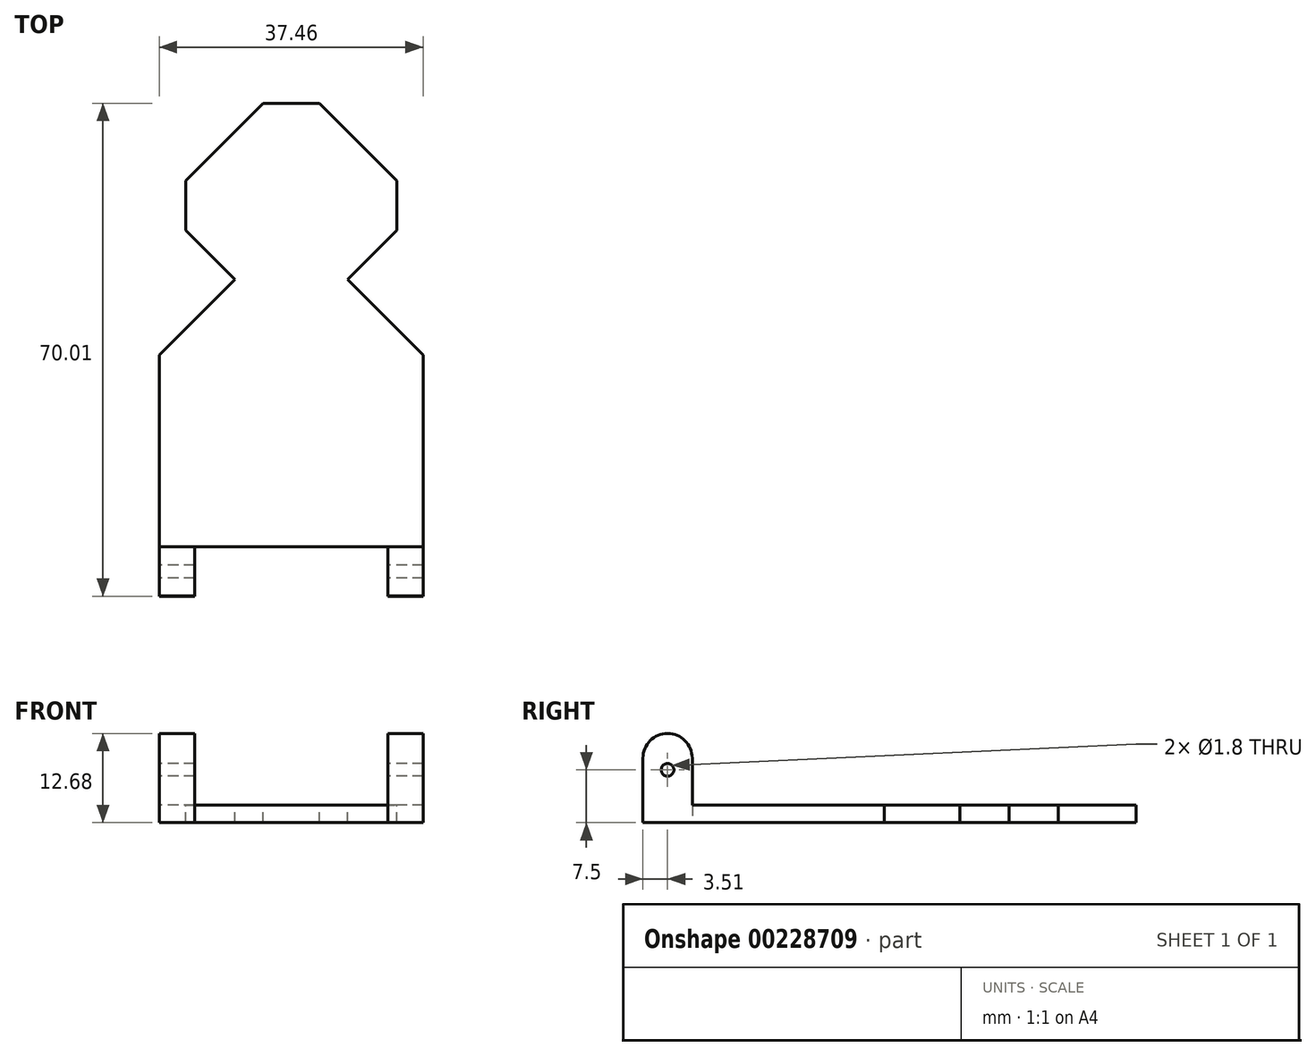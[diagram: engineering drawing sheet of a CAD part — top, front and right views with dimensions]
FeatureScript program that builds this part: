
annotation { "Feature Type Name" : "Feature", "Feature Type Description" : "" }
export const myFeature = defineFeature(function(context is Context, id is Id, definition is map)
    precondition{}
    {
        {
            var Q0;
            Q0=qCreatedBy(makeId("Right.planeOp"),FACE);
            var sketch = newSketch(context, id + "F0", { "sketchPlane" : qUnion([Q0])});
            skLineSegment(sketch, "E0.top", {"start": v(35, 2.5) * mm, "end": v(-35, 2.5) * mm});
            skLineSegment(sketch, "E0.left", {"start": v(35, 0) * mm, "end": v(35, 2.5) * mm});
            skPoint(sketch, "E0.middle", {"position": v(0, 0) * mm});
            skLineSegment(sketch, "E1.bottom", {"start": v(-28, 2.5) * mm, "end": v(-35, 2.5) * mm});
            skLineSegment(sketch, "E1.left", {"start": v(-28, 2.5) * mm, "end": v(-28, 9.18) * mm});
            skLineSegment(sketch, "E1.right", {"start": v(-35, 2.5) * mm, "end": v(-35, 9.18) * mm});
            skCircle(sketch, "E2", {"center": v(-31.5, 7.5) * mm, "radius": 0.9 * mm});
            skArc(sketch, "E3", {"start": v(-28, 9.18) * mm, "mid": v(-31.5, 12.68) * mm, "end": v(-35, 9.18) * mm});
            skLineSegment(sketch, "E4", {"start": v(35, 0) * mm, "end": v(-35, 0) * mm});
            skLineSegment(sketch, "E5", {"start": v(-35, 0) * mm, "end": v(-35, 2.5) * mm});
            skSolve(sketch);
        }
        {
            var Q0;
            {var subQ1=sQuery(id+"F0.wireOp",EDGE,"E1.left");Q0=makeQuery(id+"F0.imprint","IMPRINT",FACE,{"disambiguationData":[TD([[makeQuery(id+"F0.imprint","IMPRINT",EDGE,{"derivedFrom":subQ1}),1.0]])]});}
            var Q1;
            {var subQ0=sQuery(id+"F0.wireOp",EDGE,"E0.left");Q1=makeQuery(id+"F0.imprint","IMPRINT",FACE,{"disambiguationData":[TD([[makeQuery(id+"F0.imprint","IMPRINT",EDGE,{"derivedFrom":subQ0}),1.0]])]});}
            extrude(context, id + "F1", {"entities" : qUnion([Q0, Q1]), "depth" : 18.73 * mm, "hasSecondDirection" : true, "secondDirectionOppositeDirection" : true, "secondDirectionDepth" : 18.73 * mm});
        }
        {
            var Q0;
            Q0=qCreatedBy(makeId("Top.planeOp"),FACE);
            var sketch = newSketch(context, id + "F2", { "sketchPlane" : qUnion([Q0])});
            skLineSegment(sketch, "E6.bottom", {"start": v(13.73, -28) * mm, "end": v(-13.73, -28) * mm});
            skLineSegment(sketch, "E6.top", {"start": v(13.73, -38) * mm, "end": v(-13.73, -38) * mm});
            skLineSegment(sketch, "E6.left", {"start": v(13.73, -28) * mm, "end": v(13.73, -38) * mm});
            skLineSegment(sketch, "E6.right", {"start": v(-13.73, -28) * mm, "end": v(-13.73, -38) * mm});
            skPoint(sketch, "E6.middle", {"position": v(0, -33) * mm});
            skLineSegment(sketch, "E7.bottom", {"start": v(-15, 10) * mm, "end": v(-25, 10) * mm});
            skLineSegment(sketch, "E7.top", {"start": v(-15, 31) * mm, "end": v(-25, 31) * mm});
            skLineSegment(sketch, "E7.left", {"start": v(-15, 10) * mm, "end": v(-15, 31) * mm});
            skLineSegment(sketch, "E7.right", {"start": v(-25, 10) * mm, "end": v(-25, 31) * mm});
            skPoint(sketch, "E7.middle", {"position": v(-20, 20.5) * mm});
            skLineSegment(sketch, "E8.MirrorCS", {"start": v(15, 10) * mm, "end": v(15, 31) * mm});
            skLineSegment(sketch, "E9.MirrorCS", {"start": v(15, 10) * mm, "end": v(25, 10) * mm});
            skLineSegment(sketch, "E10.MirrorCS", {"start": v(25, 10) * mm, "end": v(25, 31) * mm});
            skLineSegment(sketch, "E11.MirrorCS", {"start": v(15, 31) * mm, "end": v(25, 31) * mm});
            skLineSegment(sketch, "E12", {"start": v(-15, 24) * mm, "end": v(-8, 31) * mm});
            skLineSegment(sketch, "E13", {"start": v(-8, 31) * mm, "end": v(-15, 31) * mm});
            skLineSegment(sketch, "E14", {"start": v(-15, 10) * mm, "end": v(-8, 10) * mm});
            skLineSegment(sketch, "E15", {"start": v(-8, 10) * mm, "end": v(-15, 17) * mm});
            skLineSegment(sketch, "E16.MirrorCS", {"start": v(8, 31) * mm, "end": v(15, 31) * mm});
            skLineSegment(sketch, "E17.MirrorCS", {"start": v(15, 24) * mm, "end": v(8, 31) * mm});
            skLineSegment(sketch, "E18.MirrorCS", {"start": v(8, 10) * mm, "end": v(15, 17) * mm});
            skLineSegment(sketch, "E19.MirrorCS", {"start": v(15, 10) * mm, "end": v(8, 10) * mm});
            skLineSegment(sketch, "E20", {"start": v(-8, 31) * mm, "end": v(-1, 38) * mm});
            skLineSegment(sketch, "E21", {"start": v(-1, 38) * mm, "end": v(-25, 38) * mm});
            skLineSegment(sketch, "E22", {"start": v(-25, 38) * mm, "end": v(-25, 31) * mm});
            skLineSegment(sketch, "E23.MirrorCS", {"start": v(8, 31) * mm, "end": v(1, 38) * mm});
            skLineSegment(sketch, "E24.MirrorCS", {"start": v(1, 38) * mm, "end": v(25, 38) * mm});
            skLineSegment(sketch, "E25.MirrorCS", {"start": v(25, 38) * mm, "end": v(25, 31) * mm});
            skLineSegment(sketch, "E26", {"start": v(-8, 10) * mm, "end": v(-25, -7) * mm});
            skLineSegment(sketch, "E27", {"start": v(-25, -7) * mm, "end": v(-25, 10) * mm});
            skLineSegment(sketch, "E28.MirrorCS", {"start": v(8, 10) * mm, "end": v(25, -7) * mm});
            skLineSegment(sketch, "E29.MirrorCS", {"start": v(25, -7) * mm, "end": v(25, 10) * mm});
            skSolve(sketch);
        }
        {
            var Q0;
            Q0=makeQuery(id+"F2.imprint","IMPRINT",FACE,{"disambiguationData":[TD([[makeQuery(id+"F2.imprint","IMPRINT",EDGE,{"derivedFrom":sQuery(id+"F2.wireOp",EDGE,"E6.bottom")}),1.0]])]});
            extrude(context, id + "F3", {"entities" : qUnion([Q0]), "operationType" : NewBodyOperationType.REMOVE, "depth" : 25 * mm, "hasSecondDirection" : true, "secondDirectionOppositeDirection" : true, "secondDirectionDepth" : 25 * mm});
        }
        {
            var Q0;
            Q0=makeQuery(id+"F2.imprint","IMPRINT",FACE,{"disambiguationData":[TD([[makeQuery(id+"F2.imprint","IMPRINT",EDGE,{"derivedFrom":sQuery(id+"F2.wireOp",EDGE,"E8.MirrorCS")}),-1.0]])]});
            var Q1;
            Q1=makeQuery(id+"F2.imprint","IMPRINT",FACE,{"disambiguationData":[TD([[makeQuery(id+"F2.imprint","IMPRINT",EDGE,{"derivedFrom":sQuery(id+"F2.wireOp",EDGE,"E7.bottom")}),-1.0]])]});
            var Q2;
            {var subQ0=sQuery(id+"F2.wireOp",EDGE,"E14");Q2=makeQuery(id+"F2.imprint","IMPRINT",FACE,{"disambiguationData":[TD([[makeQuery(id+"F2.imprint","IMPRINT",EDGE,{"derivedFrom":subQ0}),1.0]])]});}
            var Q3;
            {var subQ2=sQuery(id+"F2.wireOp",EDGE,"E12");Q3=makeQuery(id+"F2.imprint","IMPRINT",FACE,{"disambiguationData":[TD([[makeQuery(id+"F2.imprint","IMPRINT",EDGE,{"derivedFrom":subQ2}),1.0]])]});}
            var Q4;
            {var subQ2=sQuery(id+"F2.wireOp",EDGE,"E18.MirrorCS");Q4=makeQuery(id+"F2.imprint","IMPRINT",FACE,{"disambiguationData":[TD([[makeQuery(id+"F2.imprint","IMPRINT",EDGE,{"derivedFrom":subQ2}),-1.0]])]});}
            var Q5;
            {var subQ0=sQuery(id+"F2.wireOp",EDGE,"E16.MirrorCS");Q5=makeQuery(id+"F2.imprint","IMPRINT",FACE,{"disambiguationData":[TD([[makeQuery(id+"F2.imprint","IMPRINT",EDGE,{"derivedFrom":subQ0}),-1.0]])]});}
            var Q6;
            Q6=makeQuery(id+"F2.imprint","IMPRINT",FACE,{"disambiguationData":[TD([[makeQuery(id+"F2.imprint","IMPRINT",EDGE,{"derivedFrom":sQuery(id+"F2.wireOp",EDGE,"E11.MirrorCS")}),1.0]])]});
            var Q7;
            Q7=makeQuery(id+"F2.imprint","IMPRINT",FACE,{"disambiguationData":[TD([[makeQuery(id+"F2.imprint","IMPRINT",EDGE,{"derivedFrom":sQuery(id+"F2.wireOp",EDGE,"E9.MirrorCS")}),-1.0]])]});
            var Q8;
            Q8=makeQuery(id+"F2.imprint","IMPRINT",FACE,{"disambiguationData":[TD([[makeQuery(id+"F2.imprint","IMPRINT",EDGE,{"derivedFrom":sQuery(id+"F2.wireOp",EDGE,"E7.bottom")}),1.0]])]});
            var Q9;
            Q9=makeQuery(id+"F2.imprint","IMPRINT",FACE,{"disambiguationData":[TD([[makeQuery(id+"F2.imprint","IMPRINT",EDGE,{"derivedFrom":sQuery(id+"F2.wireOp",EDGE,"E7.top")}),-1.0]])]});
            extrude(context, id + "F4", {"entities" : qUnion([Q0, Q1, Q2, Q3, Q4, Q5, Q6, Q7, Q8, Q9]), "operationType" : NewBodyOperationType.REMOVE, "oppositeDirection" : true, "depth" : 5 * mm, "hasSecondDirection" : true, "secondDirectionOppositeDirection" : false, "secondDirectionDepth" : 5 * mm});
        }
    });
